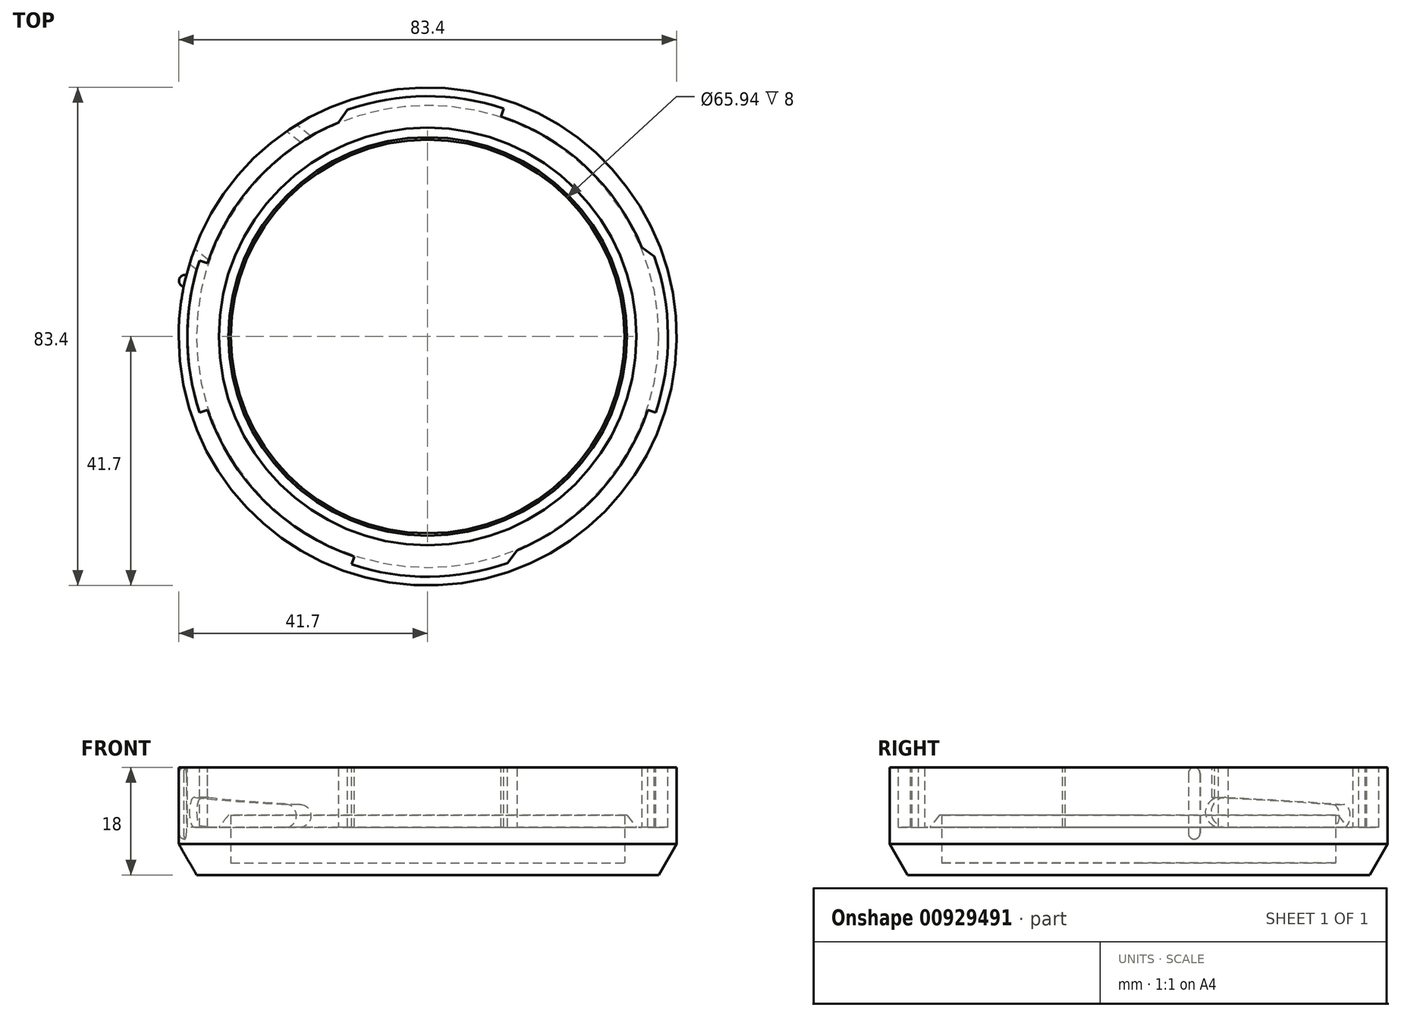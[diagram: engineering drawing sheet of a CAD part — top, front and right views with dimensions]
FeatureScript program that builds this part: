
annotation { "Feature Type Name" : "Feature", "Feature Type Description" : "" }
export const myFeature = defineFeature(function(context is Context, id is Id, definition is map)
    precondition{}
    {
        {
            var Q0;
            Q0=qCreatedBy(makeId("Front.planeOp"),FACE);
            var sketch = newSketch(context, id + "F0", { "sketchPlane" : qUnion([Q0])});
            skLineSegment(sketch, "E0", {"start": v(0, 0) * mm, "end": v(41.7, 0) * mm});
            skLineSegment(sketch, "E1", {"start": v(0, 0) * mm, "end": v(0, 2) * mm});
            skLineSegment(sketch, "E2", {"start": v(41.7, 0) * mm, "end": v(41.7, 18) * mm});
            skLineSegment(sketch, "E3", {"start": v(41.7, 18) * mm, "end": v(38.85, 18) * mm});
            skLineSegment(sketch, "E4", {"start": v(38.85, 18) * mm, "end": v(38.85, 8) * mm});
            skLineSegment(sketch, "E5", {"start": v(38.85, 8) * mm, "end": v(34.97, 8) * mm});
            skLineSegment(sketch, "E6", {"start": v(34.97, 8) * mm, "end": v(34.97, 10) * mm});
            skLineSegment(sketch, "E7", {"start": v(34.97, 10) * mm, "end": v(32.97, 10) * mm});
            skLineSegment(sketch, "E8", {"start": v(32.97, 10) * mm, "end": v(32.97, 2) * mm});
            skLineSegment(sketch, "E9", {"start": v(32.97, 2) * mm, "end": v(0, 2) * mm});
            skLineSegment(sketch, "E10", {"start": v(0, 2) * mm, "end": v(0, 44.08) * mm, "construction": true});
            skSolve(sketch);
        }
        {
            var Q0;
            Q0=qSketchRegion(id+"F0",true);
            var Q1;
            Q1=sQuery(id+"F0.wireOp",EDGE,"E1");
            revolve(context, id + "F1", {"surfaceOperationType" : NewSurfaceOperationType.NEW, "entities" : qUnion([Q0]), "axis" : qUnion([Q1]), "revolveType" : RevolveType.FULL});
        }
        {
            var Q0;
            Q0=makeQuery(id+"F1.opRevolve","SWEPT_FACE",FACE,{"disambiguationData":[OSD([sQuery(id+"F0.wireOp",EDGE,"E3")])]});
            var sketch = newSketch(context, id + "F2", { "sketchPlane" : qUnion([Q0])});
            skPoint(sketch, "E11.center", {"position": v(0, 0) * mm});
            skArc(sketch, "E12.trimOffspring", {"start": v(12.73, 38.18) * mm, "mid": v(0, 40.25) * mm, "end": v(-12.73, 38.18) * mm});
            skArc(sketch, "E13.1.0", {"start": v(38.18, -12.73) * mm, "mid": v(40.25, 0) * mm, "end": v(38.18, 12.73) * mm});
            skArc(sketch, "E13.2.0", {"start": v(-12.73, -38.18) * mm, "mid": v(0, -40.25) * mm, "end": v(12.73, -38.18) * mm});
            skArc(sketch, "E13.3.0", {"start": v(-38.18, 12.73) * mm, "mid": v(-40.25, 0) * mm, "end": v(-38.18, -12.73) * mm});
            skLineSegment(sketch, "E14", {"start": v(12.73, 38.18) * mm, "end": v(12.29, 36.86) * mm});
            skLineSegment(sketch, "E15", {"start": v(-12.73, 38.18) * mm, "end": v(-12.29, 36.86) * mm});
            skLineSegment(sketch, "E16", {"start": v(38.18, 12.73) * mm, "end": v(36.86, 12.29) * mm});
            skLineSegment(sketch, "E17", {"start": v(38.18, -12.73) * mm, "end": v(36.86, -12.29) * mm});
            skArc(sketch, "E18", {"start": v(12.29, 36.86) * mm, "mid": v(0, 38.85) * mm, "end": v(-12.29, 36.86) * mm});
            skArc(sketch, "E19", {"start": v(-12.29, 36.86) * mm, "mid": v(-27.47, 27.47) * mm, "end": v(-36.86, 12.29) * mm});
            skArc(sketch, "E20", {"start": v(-36.86, 12.29) * mm, "mid": v(-38.85, 0) * mm, "end": v(-36.86, -12.29) * mm});
            skArc(sketch, "E21", {"start": v(-36.86, -12.29) * mm, "mid": v(-27.47, -27.47) * mm, "end": v(-12.29, -36.86) * mm});
            skArc(sketch, "E22", {"start": v(-12.29, -36.86) * mm, "mid": v(0, -38.85) * mm, "end": v(12.29, -36.86) * mm});
            skArc(sketch, "E23", {"start": v(12.29, -36.86) * mm, "mid": v(27.47, -27.47) * mm, "end": v(36.86, -12.29) * mm});
            skArc(sketch, "E24", {"start": v(36.86, -12.29) * mm, "mid": v(38.85, 0) * mm, "end": v(36.86, 12.29) * mm});
            skArc(sketch, "E25", {"start": v(36.86, 12.29) * mm, "mid": v(27.47, 27.47) * mm, "end": v(12.29, 36.86) * mm});
            skLineSegment(sketch, "E26", {"start": v(12.29, -36.86) * mm, "end": v(12.73, -38.18) * mm});
            skLineSegment(sketch, "E27", {"start": v(-12.29, -36.86) * mm, "end": v(-12.73, -38.18) * mm});
            skLineSegment(sketch, "E28", {"start": v(-36.86, -12.29) * mm, "end": v(-38.18, -12.73) * mm});
            skLineSegment(sketch, "E29", {"start": v(-36.86, 12.29) * mm, "end": v(-38.18, 12.73) * mm});
            skSolve(sketch);
        }
        {
            var Q0;
            Q0=makeQuery(id+"F2.imprint","IMPRINT",FACE,{"disambiguationData":[TD([[makeQuery(id+"F2.imprint","IMPRINT",EDGE,{"derivedFrom":sQuery(id+"F2.wireOp",EDGE,"E12.trimOffspring")}),1.0]])]});
            var Q1;
            Q1=makeQuery(id+"F2.imprint","IMPRINT",FACE,{"disambiguationData":[TD([[makeQuery(id+"F2.imprint","IMPRINT",EDGE,{"derivedFrom":sQuery(id+"F2.wireOp",EDGE,"E13.1.0")}),1.0]])]});
            var Q2;
            Q2=makeQuery(id+"F2.imprint","IMPRINT",FACE,{"disambiguationData":[TD([[makeQuery(id+"F2.imprint","IMPRINT",EDGE,{"derivedFrom":sQuery(id+"F2.wireOp",EDGE,"E13.2.0")}),1.0]])]});
            var Q3;
            Q3=makeQuery(id+"F2.imprint","IMPRINT",FACE,{"disambiguationData":[TD([[makeQuery(id+"F2.imprint","IMPRINT",EDGE,{"derivedFrom":sQuery(id+"F2.wireOp",EDGE,"E13.3.0")}),1.0]])]});
            var Q4;
            Q4=makeQuery(id+"F1.opRevolve","SWEPT_FACE",FACE,{"disambiguationData":[OSD([sQuery(id+"F0.wireOp",EDGE,"E5")])]});
            extrude(context, id + "F3", {"entities" : qUnion([Q0, Q1, Q2, Q3]), "operationType" : NewBodyOperationType.REMOVE, "endBound" : BoundingType.UP_TO_SURFACE, "oppositeDirection" : true, "depth" : 10 * mm, "endBoundEntityFace" : qUnion([Q4]), "offsetDistance" : 25 * mm});
        }
        {
            var Q0;
            Q0=makeQuery(id+"F3.boolean.opBoolean","COPY",EDGE,{"derivedFrom":makeQuery(id+"F3.opExtrude","SWEPT_EDGE",EDGE,{"disambiguationData":[OSD([sQuery(id+"F2.wireOp",EDGE,"E16"),sQuery(id+"F2.wireOp",EDGE,"E24"),sQuery(id+"F2.wireOp",EDGE,"E25")])]})});
            var Q1;
            Q1=makeQuery(id+"F3.boolean.opBoolean","COPY",EDGE,{"derivedFrom":makeQuery(id+"F3.opExtrude","SWEPT_EDGE",EDGE,{"disambiguationData":[OSD([sQuery(id+"F2.wireOp",EDGE,"E15"),sQuery(id+"F2.wireOp",EDGE,"E18"),sQuery(id+"F2.wireOp",EDGE,"E19")])]})});
            var Q2;
            Q2=makeQuery(id+"F3.boolean.opBoolean","COPY",EDGE,{"derivedFrom":makeQuery(id+"F3.opExtrude","SWEPT_EDGE",EDGE,{"disambiguationData":[OSD([sQuery(id+"F2.wireOp",EDGE,"E22"),sQuery(id+"F2.wireOp",EDGE,"E23"),sQuery(id+"F2.wireOp",EDGE,"E26")])]})});
            var Q3;
            Q3=makeQuery(id+"F3.boolean.opBoolean","COPY",EDGE,{"derivedFrom":makeQuery(id+"F3.opExtrude","SWEPT_EDGE",EDGE,{"disambiguationData":[OSD([sQuery(id+"F2.wireOp",EDGE,"E20"),sQuery(id+"F2.wireOp",EDGE,"E21"),sQuery(id+"F2.wireOp",EDGE,"E28")])]})});
            chamfer(context, id + "F4", {"entities" : qUnion([Q0, Q1, Q2, Q3]), "chamferType" : ChamferType.TWO_OFFSETS, "width1" : 3 * mm, "oppositeDirection" : false, "width2" : 2 * mm, "tangentPropagation" : true});
        }
        {
            var Q0;
            Q0=makeQuery(id+"F1.opRevolve","SWEPT_EDGE",EDGE,{"disambiguationData":[OSD([sQuery(id+"F0.wireOp",EDGE,"E6"),sQuery(id+"F0.wireOp",EDGE,"E7")])]});
            chamfer(context, id + "F5", {"entities" : qUnion([Q0]), "chamferType" : ChamferType.TWO_OFFSETS, "width1" : 2 * mm, "oppositeDirection" : false, "width2" : 1.6 * mm, "tangentPropagation" : true});
        }
        {
            var Q0;
            Q0=sQuery(id+"F0.wireOp",EDGE,"E10");
            cPlane(context, id + "F6", {"entities" : qUnion([Q0]), "cplaneType" : CPlaneType.LINE_ANGLE, "offset" : 25 * mm, "angle" : 38 * degree, "oppositeDirection" : true, "width" : 150 * mm, "height" : 150 * mm});
        }
        {
            var Q0;
            Q0=qCreatedBy(id+"F6.planeOp",FACE);
            cPlane(context, id + "F7", {"entities" : qUnion([Q0]), "cplaneType" : CPlaneType.OFFSET, "offset" : 50 * mm, "oppositeDirection" : true, "width" : 150 * mm, "height" : 150 * mm});
        }
        {
            var Q0;
            Q0=qCreatedBy(id+"F7.planeOp",FACE);
            var sketch = newSketch(context, id + "F8", { "sketchPlane" : qUnion([Q0])});
            skLineSegment(sketch, "E30.0", {"start": v(23.92, 8) * mm, "end": v(21.53, 8) * mm});
            skLineSegment(sketch, "E31", {"start": v(0, 8) * mm, "end": v(-12.5, 8) * mm});
            skLineSegment(sketch, "E32.MirrorCS", {"start": v(0, 8) * mm, "end": v(12.5, 8) * mm});
            skArc(sketch, "E33", {"start": v(12.5, 8) * mm, "mid": v(14.4, 9.9) * mm, "end": v(12.5, 11.8) * mm});
            skArc(sketch, "E34", {"start": v(-12.5, 13) * mm, "mid": v(-15, 10.5) * mm, "end": v(-12.5, 8) * mm});
            skLineSegment(sketch, "E35", {"start": v(12.5, 11.8) * mm, "end": v(-12.5, 13) * mm});
            skSolve(sketch);
        }
        {
            var Q0;
            Q0=makeQuery(id+"F8.imprint","IMPRINT",FACE,{"disambiguationData":[TD([[makeQuery(id+"F8.imprint","IMPRINT",EDGE,{"derivedFrom":sQuery(id+"F8.wireOp",EDGE,"E31")}),-1.0]])]});
            extrude(context, id + "F9", {"entities" : qUnion([Q0]), "operationType" : NewBodyOperationType.REMOVE, "depth" : 14.8 * mm, "offsetDistance" : 25 * mm});
        }
        {
            var Q0;
            Q0=makeQuery(id+"F1.opRevolve","SWEPT_EDGE",EDGE,{"disambiguationData":[OSD([sQuery(id+"F0.wireOp",EDGE,"E0"),sQuery(id+"F0.wireOp",EDGE,"E2")])]});
            chamfer(context, id + "F10", {"entities" : qUnion([Q0]), "chamferType" : ChamferType.OFFSET_ANGLE, "width" : 3 * mm, "oppositeDirection" : false, "angle" : 60 * degree, "tangentPropagation" : true});
        }
        {
            var Q0;
            Q0=qCreatedBy(makeId("Top.planeOp"),FACE);
            cPlane(context, id + "F11", {"entities" : qUnion([Q0]), "cplaneType" : CPlaneType.OFFSET, "offset" : 6 * mm, "width" : 150 * mm, "height" : 150 * mm});
        }
        {
            var Q0;
            Q0=qCreatedBy(id+"F11.planeOp",FACE);
            var sketch = newSketch(context, id + "F12", { "sketchPlane" : qUnion([Q0])});
            skCircle(sketch, "E36", {"center": v(-40.65, 9.31) * mm, "radius": 1 * mm});
            skSolve(sketch);
        }
        {
            var Q0;
            Q0=qSketchRegion(id+"F12",true);
            var Q1;
            Q1=makeQuery(id+"F1.opRevolve","SWEPT_FACE",FACE,{"disambiguationData":[OSD([sQuery(id+"F0.wireOp",EDGE,"E3")])]});
            extrude(context, id + "F13", {"entities" : qUnion([Q0]), "operationType" : NewBodyOperationType.ADD, "endBound" : BoundingType.UP_TO_SURFACE, "depth" : 12 * mm, "endBoundEntityFace" : qUnion([Q1]), "offsetDistance" : 25 * mm});
        }
        {
            var Q0;
            Q0=makeQuery(id+"F13.opExtrude","CAP_EDGE",EDGE,{"disambiguationData":[OSD([sQuery(id+"F12.wireOp",EDGE,"E36")])],"isStart":true});
            var Q1;
            Q1=makeQuery(id+"F13.opExtrude","CAP_EDGE",EDGE,{"disambiguationData":[OSD([sQuery(id+"F12.wireOp",EDGE,"E36")])],"isStart":false});
            fillet(context, id + "F14", {"entities" : qUnion([Q0, Q1]), "radius" : 1 * mm, "tangentPropagation" : true, "allowEdgeOverflow" : false});
        }
    });
